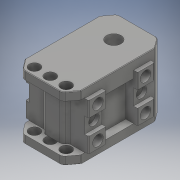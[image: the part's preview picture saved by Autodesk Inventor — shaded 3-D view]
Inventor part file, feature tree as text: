
AUTODESK INVENTOR PART (.ipt)
format: ipt  version: 2017 (Build 210142000, 142)  size: 598,016 bytes
history: native  units: mm
features: extrude x10, sketch x10, projected_geometry x8, mirror x2, chamfer x2, fillet x2, other x2, plane x1
ambient origin geometry x8: Origin, YZ Plane, XZ Plane, XY Plane, X Axis, Y Axis, Z Axis, Center Point
bodies: Solid1 (feature_tree)
feature tree (37):
  extrude  "Extrusion1"  Depth=24.0mm
  extrude  "Extrusion2"  Depth=6.0mm
  extrude  "Extrusion3"  Depth=3.0mm
  extrude  "Extrusion4"  Depth=24.0mm TaperAngle=0.0deg
  extrude  "Extrusion5"  Depth=12.0mm
  extrude  "Extrusion6"  Depth=5.5mm
  extrude  "Extrusion7"  Depth=3.0mm TaperAngle=0.0deg
  extrude  "Extrusion8"  Depth=4.0mm
  plane  "Work Plane1"
  mirror  "Mirror1"
  extrude  "Extrusion9"  Depth=4.0mm
  mirror  "Mirror2"
  chamfer  "Chamfer2"  Distance=12.0mm
  fillet  "Fillet1"  Radius=6.0mm
  extrude  "Extrusion10"  Depth=24.0mm
  fillet  "Fillet2"  Radius=17.6mm
  chamfer  "Chamfer3"  Distance=5.0mm
  sketch  "Sketch1"  dims[d0=36.0mm d1=24.0mm]
  other  "Image1"
  sketch  "Sketch2"  dims[d15=6.0mm d17=6.0mm]
  other  "Image2"
  projected_geometry  "Projected Loop1"
  projected_geometry  "Projected Loop2"
  sketch  "Sketch3"  dims[d19=24.0mm d20=0.0mm d28=3.0mm]
  sketch  "Sketch4"  dims[d29=3.0mm d30=24.0mm d31=0.0mm]
  sketch  "Sketch5"  dims[d32=12.0mm d34=1.7mm d35=1.7mm]
  sketch  "Sketch6"  dims[d36=5.6mm d37=5.5mm]
  sketch  "Sketch7"  dims[d41=24.0mm d42=0.0mm d43=3.0mm d44=0.0mm]
  sketch  "Sketch8"  dims[d45=3.0mm d46=0.0mm d48=4.0mm]
  sketch  "Sketch9"  dims[d49=3.0mm d50=4.0mm]
  sketch  "Sketch10"  dims[d51=4.0mm d52=12.0mm d53=6.0mm d59=24.0mm d60=17.6mm d61=5.0mm d62=0.0mm d63=4.0mm d64=4.0mm d65=4.0mm d66=24.0mm d67=3.0mm d68=0.0mm d79=3.0mm d80=0.0mm d83=3.0mm d84=0.0mm d88=6.0mm d89=0.8mm d90=2.0mm d91=45.0deg d92=2.0mm d93=7.5mm d94=1.5mm d95=0.0mm d96=1.5mm d97=5.5mm d98=0.2mm d99=2.0mm d100=45.0deg d102=25.0mm d103=12.0mm d104=21.0mm d107=15.0mm d109=9.0mm d110=24.0mm d111=12.0mm d123=6.283185mm d127=36.0mm d132=3.5mm d133=4.0mm d134=6.0mm d135=18.0mm d136=9.0mm d137=30.0mm d139=6.0mm d140=20.0mm d142=18.0mm]
  projected_geometry  "Projected Loop3"
  projected_geometry  "Projected Loop4"
  projected_geometry  "Projected Loop11"
  projected_geometry  "Projected Loop12"
  projected_geometry  "Projected Loop13"
  projected_geometry  "Projected Loop14"
